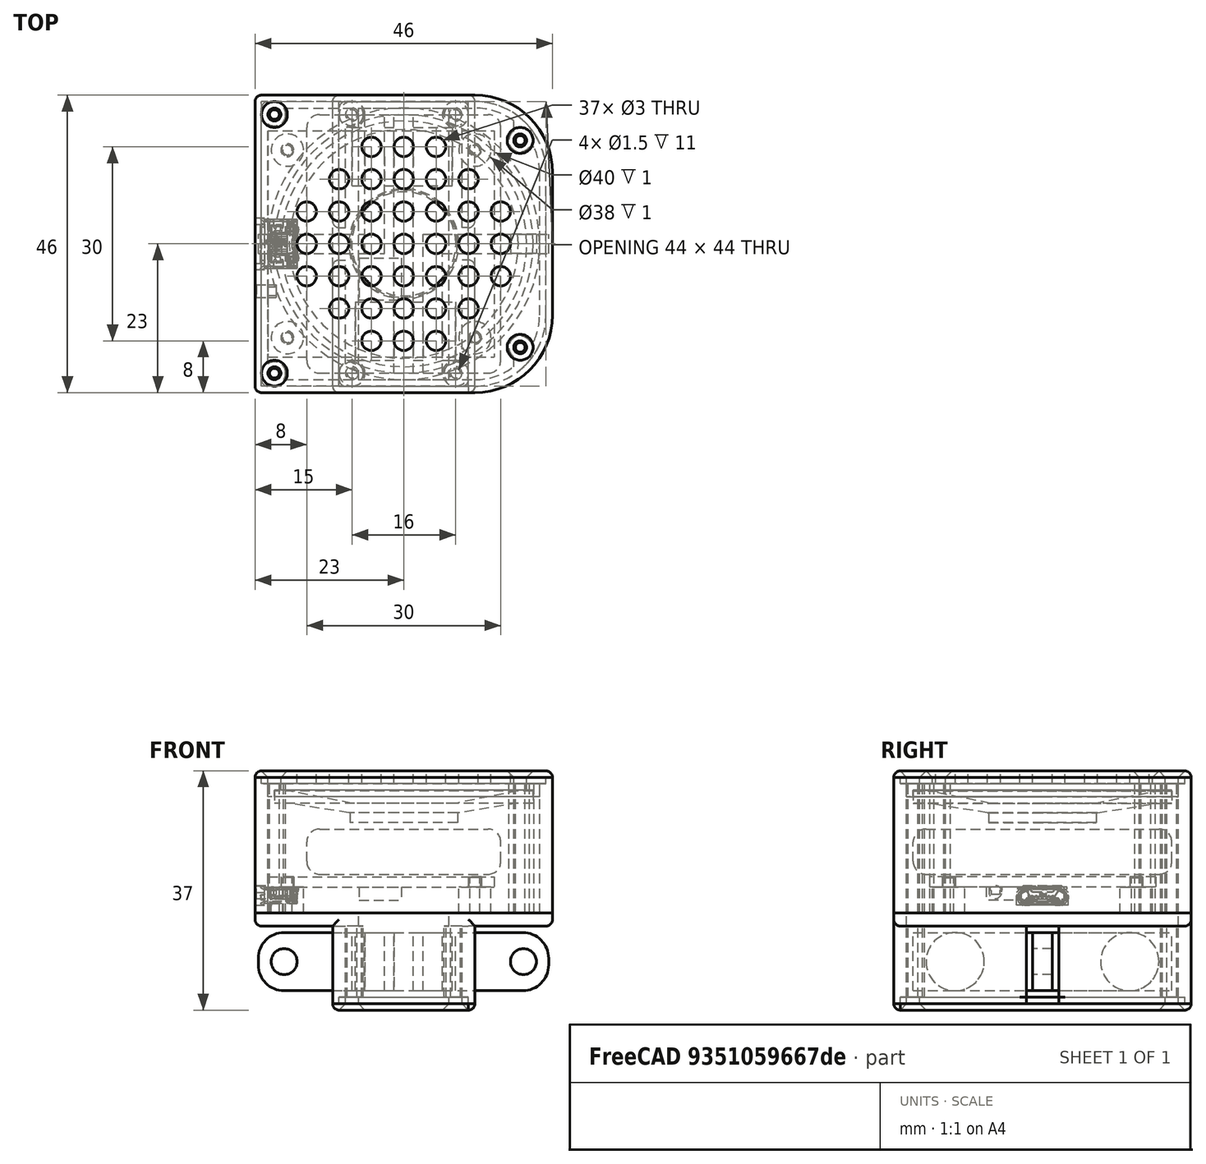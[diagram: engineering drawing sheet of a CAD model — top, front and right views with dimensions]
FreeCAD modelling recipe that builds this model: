
FCSTD DOCUMENT  (FreeCAD 0.19R)
Label: NoPullShit
License: All rights reserved
LicenseURL: http://en.wikipedia.org/wiki/All_rights_reserved
objects: Part::Cylinder×88, Part::Box×36, Part::Cut×32, Part::Fillet×21, Part::MultiFuse×20, Part::Chamfer×3, Part::Cone×2, Part::Feature×1
note: 203 computed .brp shape members not serialized (recipe doc carries the construction recipe); baked Part::Feature solids carry a one-line shape summary decoded from their .brp

FEATURE [Part::Box] Box  label="BatteryCube"
  AttacherType = Attacher::AttachEngine3D
  Height = 7
  Length = 30
  Placement = pos=(-15,-20,21) rot=(0,0,1;0rad)
  Width = 40
FEATURE [Part::Box] Box001  label="FR4"
  AttacherType = Attacher::AttachEngine3D
  Height = 1.6
  Length = 35
  Width = 35
FEATURE [Part::Feature] Solid  label="10103594_AFCI_SW0001"
  Placement = pos=(3,17.5,3.8) rot=(0.57735,0.57735,-0.57735;4.18879rad)
  shape: bbox 6.034 x 8.041 x 3.601 mm, 793 faces (baked)
FEATURE [Part::Box] Box002  label="LEDa"
  AttacherType = Attacher::AttachEngine3D
  Height = 0.5
  Length = 1.25
  Width = 2
FEATURE [Part::Box] Box003  label="LEDb"
  AttacherType = Attacher::AttachEngine3D
  Height = 0.6
  Length = 1.25
  Placement = pos=(0,0.35,0.5) rot=(0,0,1;0rad)
  Width = 1.3
FEATURE [Part::MultiFuse] Fusion001  label="LED"
  Placement = pos=(0,23.792,1.6) rot=(0,0,1;0rad)
  Shapes = -> [Box002,Box003]
FEATURE [Part::Cylinder] Cylinder002  label="MH1"
  Angle = 360
  AttacherType = Attacher::AttachEngine3D
  Height = 1.6
  Placement = pos=(3,3,0) rot=(0,0,1;0rad)
  Radius = 1
FEATURE [Part::Cylinder] Cylinder003  label="MH2"
  Angle = 360
  AttacherType = Attacher::AttachEngine3D
  Height = 1.6
  Placement = pos=(32,3,0) rot=(0,0,1;0rad)
  Radius = 1
FEATURE [Part::Cylinder] Cylinder004  label="MH3"
  Angle = 360
  AttacherType = Attacher::AttachEngine3D
  Height = 1.6
  Placement = pos=(3,32,0) rot=(0,0,1;0rad)
  Radius = 1
FEATURE [Part::Cylinder] Cylinder005  label="MH4"
  Angle = 360
  AttacherType = Attacher::AttachEngine3D
  Height = 1.6
  Placement = pos=(32,32,0) rot=(0,0,1;0rad)
  Radius = 1
FEATURE [Part::MultiFuse] Fusion002  label="Holes"
  Shapes = -> [Cylinder002,Cylinder003,Cylinder004,Cylinder005]
FEATURE [Part::Cut] Cut
  Base = -> Box001
  Tool = -> Fusion002
FEATURE [Part::Box] Box004  label="MCU"
  AttacherType = Attacher::AttachEngine3D
  Height = 2
  Length = 6.5
  Placement = pos=(14.1,19.7,1.6) rot=(0,0,1;0rad)
  Width = 6.5
FEATURE [Part::MultiFuse] Fusion003  label="Board"
  Placement = pos=(-21,17.5,20.6) rot=(1,0,0;3.14159rad)
  Shapes = -> [Box004,Solid,Fusion001,Cut]
FEATURE [Part::Box] Box005  label="Cube"
  AttacherType = Attacher::AttachEngine3D
  Height = 9
  Length = 3
  Width = 40
FEATURE [Part::Box] Box006  label="Cube001"
  AttacherType = Attacher::AttachEngine3D
  Height = 9
  Length = 3
  Placement = pos=(4.5,0,0) rot=(0,0,1;0rad)
  Width = 21.5
FEATURE [Part::Box] Box007  label="Cube002"
  AttacherType = Attacher::AttachEngine3D
  Height = 9
  Length = 3
  Placement = pos=(-4.5,18.5,0) rot=(0,0,1;0rad)
  Width = 21.5
FEATURE [Part::Cylinder] Cylinder006
  Angle = 360
  AttacherType = Attacher::AttachEngine3D
  Height = 15.5
  Placement = pos=(-6,6.5,4.5) rot=(0,1,0;1.5708rad)
  Radius = 4.5
FEATURE [Part::Cylinder] Cylinder007
  Angle = 360
  AttacherType = Attacher::AttachEngine3D
  Height = 15.5
  Placement = pos=(-6.5,33.5,4.5) rot=(0,1,0;1.5708rad)
  Radius = 4.5
FEATURE [Part::Box] Box008  label="Cube003"
  AttacherType = Attacher::AttachEngine3D
  Height = 9
  Length = 16.4
  Placement = pos=(-21,18.5,0) rot=(0,0,1;0rad)
  Width = 3
FEATURE [Part::Box] Box009  label="Cube004"
  AttacherType = Attacher::AttachEngine3D
  Height = 9
  Length = 16.4
  Placement = pos=(7.5,18.5,0) rot=(0,0,1;0rad)
  Width = 3
FEATURE [Part::MultiFuse] Fusion004  label="Solid"
  Placement = pos=(-1.5,0,0) rot=(0,0,1;0rad)
  Shapes = -> [Box005,Box006,Box007,Cylinder006,Cylinder007,Box008,Box009]
FEATURE [Part::Cylinder] Cylinder008
  Angle = 360
  AttacherType = Attacher::AttachEngine3D
  Height = 10
  Placement = pos=(-18.5,25,4.5) rot=(1,0,0;1.5708rad)
  Radius = 2
FEATURE [Part::Cylinder] Cylinder009
  Angle = 360
  AttacherType = Attacher::AttachEngine3D
  Height = 10
  Placement = pos=(18.5,25,4.5) rot=(1,0,0;1.5708rad)
  Radius = 2
FEATURE [Part::MultiFuse] Fusion005  label="Holes001"
  Shapes = -> [Cylinder009,Cylinder008]
FEATURE [Part::Cut] Cut001  label="Solid001"
  Base = -> Fusion004
  Placement = pos=(0,-20,3) rot=(0,0,1;0rad)
  Tool = -> Fusion005
FEATURE [Part::Cylinder] Cylinder029
  Angle = 360
  AttacherType = Attacher::AttachEngine3D
  Height = 4
  Placement = pos=(-18,-14.5,15) rot=(0,0,1;0rad)
  Radius = 2.5
FEATURE [Part::Cylinder] Cylinder030
  Angle = 360
  AttacherType = Attacher::AttachEngine3D
  Height = 1.5
  Placement = pos=(-18,-14.5,19) rot=(0,0,1;0rad)
  Radius = 0.9
FEATURE [Part::Cylinder] Cylinder031
  Angle = 360
  AttacherType = Attacher::AttachEngine3D
  Height = 5.5
  Placement = pos=(-18,-14.5,15) rot=(0,0,1;0rad)
  Radius = 0.75
FEATURE [Part::MultiFuse] Fusion006
  Shapes = -> [Cylinder029,Cylinder030]
FEATURE [Part::Cut] Cut006  label="Support1"
  Base = -> Fusion006
  Tool = -> Cylinder031
FEATURE [Part::Cylinder] Cylinder032
  Angle = 360
  AttacherType = Attacher::AttachEngine3D
  Height = 4
  Placement = pos=(-18,-14.5,15) rot=(0,0,1;0rad)
  Radius = 2.5
FEATURE [Part::Cylinder] Cylinder033
  Angle = 360
  AttacherType = Attacher::AttachEngine3D
  Height = 1.5
  Placement = pos=(-18,-14.5,19) rot=(0,0,1;0rad)
  Radius = 0.9
FEATURE [Part::MultiFuse] Fusion007
  Shapes = -> [Cylinder032,Cylinder033]
FEATURE [Part::Cylinder] Cylinder034
  Angle = 360
  AttacherType = Attacher::AttachEngine3D
  Height = 5.5
  Placement = pos=(-18,-14.5,15) rot=(0,0,1;0rad)
  Radius = 0.75
FEATURE [Part::Cut] Cut007  label="Support2"
  Base = -> Fusion007
  Placement = pos=(29,0,0) rot=(0,0,1;0rad)
  Tool = -> Cylinder034
FEATURE [Part::Cylinder] Cylinder035
  Angle = 360
  AttacherType = Attacher::AttachEngine3D
  Height = 4
  Placement = pos=(-18,-14.5,15) rot=(0,0,1;0rad)
  Radius = 2.5
FEATURE [Part::Cylinder] Cylinder036
  Angle = 360
  AttacherType = Attacher::AttachEngine3D
  Height = 1.5
  Placement = pos=(-18,-14.5,19) rot=(0,0,1;0rad)
  Radius = 0.9
FEATURE [Part::MultiFuse] Fusion008
  Shapes = -> [Cylinder035,Cylinder036]
FEATURE [Part::Cylinder] Cylinder037
  Angle = 360
  AttacherType = Attacher::AttachEngine3D
  Height = 5.5
  Placement = pos=(-18,-14.5,15) rot=(0,0,1;0rad)
  Radius = 0.75
FEATURE [Part::Cut] Cut008  label="Support3"
  Base = -> Fusion008
  Placement = pos=(29,29,0) rot=(0,0,1;0rad)
  Tool = -> Cylinder037
FEATURE [Part::Cylinder] Cylinder038
  Angle = 360
  AttacherType = Attacher::AttachEngine3D
  Height = 4
  Placement = pos=(-18,-14.5,15) rot=(0,0,1;0rad)
  Radius = 2.5
FEATURE [Part::Cylinder] Cylinder039
  Angle = 360
  AttacherType = Attacher::AttachEngine3D
  Height = 1.5
  Placement = pos=(-18,-14.5,19) rot=(0,0,1;0rad)
  Radius = 0.9
FEATURE [Part::MultiFuse] Fusion009
  Shapes = -> [Cylinder038,Cylinder039]
FEATURE [Part::Cylinder] Cylinder040
  Angle = 360
  AttacherType = Attacher::AttachEngine3D
  Height = 5.5
  Placement = pos=(-18,-14.5,15) rot=(0,0,1;0rad)
  Radius = 0.75
FEATURE [Part::Cut] Cut009  label="Support4"
  Base = -> Fusion009
  Placement = pos=(0,29,0) rot=(0,0,1;0rad)
  Tool = -> Cylinder040
FEATURE [Part::Fillet] Fillet  label="Battery"
  Base = -> Box
  Edges = 12 edges r=2: [Edge1,Edge2,Edge3,Edge4,Edge5,Edge6,Edge7,Edge8,Edge9,Edge10,Edge11,Edge12]
FEATURE [Part::MultiFuse] Fusion022  label="PcbSupport"
  Shapes = -> [Cut006,Cut007,Cut008,Cut009]
FEATURE [Part::Fillet] Fillet009  label="LoadCell"
  Base = -> Cut001
  Edges = 4 edges r=4: [Edge82,Edge89,Edge102,Edge104]
FEATURE [Part::Cylinder] Cylinder128
  Angle = 360
  AttacherType = Attacher::AttachEngine3D
  Height = 1.9
  Radius = 20
FEATURE [Part::Cone] Cone001
  Angle = 360
  AttacherType = Attacher::AttachEngine3D
  Height = 1.5
  Placement = pos=(0,0,1.9) rot=(0,0,1;0rad)
  Radius1 = 17.7
  Radius2 = 8.5
FEATURE [Part::Cylinder] Cylinder129
  Angle = 360
  AttacherType = Attacher::AttachEngine3D
  Height = 1.5
  Placement = pos=(0,0,3.4) rot=(0,0,1;0rad)
  Radius = 8.3
FEATURE [Part::Cone] Cone002
  Angle = 360
  AttacherType = Attacher::AttachEngine3D
  Height = 2.5
  Radius1 = 17.7
  Radius2 = 5
FEATURE [Part::Cut] Cut034
  Base = -> Cylinder128
  Tool = -> Cone002
FEATURE [Part::MultiFuse] Fusion025  label="Speaker"
  Placement = pos=(0,0,33.9) rot=(1,0,0;3.14159rad)
  Shapes = -> [Cone001,Cylinder129,Cut034]
FEATURE [Part::Box] Box078  label="Cube073"
  AttacherType = Attacher::AttachEngine3D
  Height = 2
  Length = 22
  Placement = pos=(-11,-23,0) rot=(0,0,1;0rad)
  Width = 46
FEATURE [Part::Cylinder] Cylinder209
  Angle = 360
  AttacherType = Attacher::AttachEngine3D
  Height = 11
  Placement = pos=(-8,-20,-3) rot=(0,0,1;0rad)
  Radius = 1
FEATURE [Part::Cylinder] Cylinder210
  Angle = 360
  AttacherType = Attacher::AttachEngine3D
  Height = 11
  Placement = pos=(8,-20,-3) rot=(0,0,1;0rad)
  Radius = 1
FEATURE [Part::Cylinder] Cylinder211
  Angle = 360
  AttacherType = Attacher::AttachEngine3D
  Height = 11
  Placement = pos=(-8,20,-3) rot=(0,0,1;0rad)
  Radius = 1
FEATURE [Part::Cylinder] Cylinder212
  Angle = 360
  AttacherType = Attacher::AttachEngine3D
  Height = 11
  Placement = pos=(8,20,-3) rot=(0,0,1;0rad)
  Radius = 1
FEATURE [Part::MultiFuse] Fusion039
  Shapes = -> [Cylinder209,Cylinder210,Cylinder211,Cylinder212]
FEATURE [Part::Cut] Cut063
  Base = -> Box078
  Tool = -> Fusion039
FEATURE [Part::Chamfer] Chamfer008
  Base = -> Cut063
  Edges = 4 edges r=1: [Edge17,Edge18,Edge19,Edge20]
FEATURE [Part::Fillet] Fillet028
  Base = -> Chamfer008
  Edges = 8 edges r=1: [Edge2,Edge3,Edge4,Edge5,Edge11,Edge13,Edge14,Edge16]
FEATURE [Part::Box] Box079  label="Cube074"
  AttacherType = Attacher::AttachEngine3D
  Height = 1
  Length = 20
  Placement = pos=(-10,-22,1) rot=(0,0,1;0rad)
  Width = 44
FEATURE [Part::Box] Box080  label="Cube075"
  AttacherType = Attacher::AttachEngine3D
  Height = 1
  Length = 22
  Placement = pos=(-11,-23,1) rot=(0,0,1;0rad)
  Width = 46
FEATURE [Part::Cut] Cut064
  Base = -> Box080
  Tool = -> Box079
FEATURE [Part::Box] Box085  label="Cube080"
  AttacherType = Attacher::AttachEngine3D
  Height = 2
  Length = 14
  Placement = pos=(-7,-21,13) rot=(0,0,1;0rad)
  Width = 42
FEATURE [Part::Box] Box086  label="Cube081"
  AttacherType = Attacher::AttachEngine3D
  Height = 2
  Length = 46
  Placement = pos=(-23,-23,13) rot=(0,0,1;0rad)
  Width = 46
FEATURE [Part::Fillet] Fillet030
  Base = -> Box086
  Edges = 2 edges r=1: [Edge1,Edge3]
FEATURE [Part::Fillet] Fillet029
  Base = -> Fillet030
  Edges = 2 edges r=12: [Edge17,Edge18]
FEATURE [Part::Cut] Cut066
  Base = -> Fillet029
  Tool = -> Box085
FEATURE [Part::Box] Box087  label="Cube082"
  AttacherType = Attacher::AttachEngine3D
  Height = 12
  Length = 22
  Placement = pos=(-11,-23,1) rot=(0,0,1;0rad)
  Width = 2
FEATURE [Part::Box] Box088  label="Cube083"
  AttacherType = Attacher::AttachEngine3D
  Height = 12
  Length = 22
  Placement = pos=(-11,21,1) rot=(0,0,1;0rad)
  Width = 2
FEATURE [Part::Box] Box089  label="Cube084"
  AttacherType = Attacher::AttachEngine3D
  Height = 12
  Length = 2
  Placement = pos=(-11,-23,1) rot=(0,0,1;0rad)
  Width = 20.5
FEATURE [Part::Box] Box090  label="Cube085"
  AttacherType = Attacher::AttachEngine3D
  Height = 12
  Length = 2
  Placement = pos=(9,-23,1) rot=(0,0,1;0rad)
  Width = 20.5
FEATURE [Part::Box] Box091  label="Cube086"
  AttacherType = Attacher::AttachEngine3D
  Height = 12
  Length = 2
  Placement = pos=(-11,2.5,1) rot=(0,0,1;0rad)
  Width = 20.5
FEATURE [Part::Box] Box092  label="Cube087"
  AttacherType = Attacher::AttachEngine3D
  Height = 12
  Length = 2
  Placement = pos=(9,2.5,1) rot=(0,0,1;0rad)
  Width = 20.5
FEATURE [Part::Cylinder] Cylinder213
  Angle = 360
  AttacherType = Attacher::AttachEngine3D
  Height = 11
  Placement = pos=(-8,-20,2) rot=(0,0,1;0rad)
  Radius = 1.75
FEATURE [Part::Cylinder] Cylinder214
  Angle = 360
  AttacherType = Attacher::AttachEngine3D
  Height = 11
  Placement = pos=(8,-20,2) rot=(0,0,1;0rad)
  Radius = 1.75
FEATURE [Part::Cylinder] Cylinder215
  Angle = 360
  AttacherType = Attacher::AttachEngine3D
  Height = 11
  Placement = pos=(-8,20,2) rot=(0,0,1;0rad)
  Radius = 1.75
FEATURE [Part::Cylinder] Cylinder216
  Angle = 360
  AttacherType = Attacher::AttachEngine3D
  Height = 11
  Placement = pos=(8,20,2) rot=(0,0,1;0rad)
  Radius = 1.75
FEATURE [Part::Cylinder] Cylinder217
  Angle = 360
  AttacherType = Attacher::AttachEngine3D
  Height = 11
  Placement = pos=(-8,-20,2) rot=(0,0,1;0rad)
  Radius = 0.75
FEATURE [Part::Cylinder] Cylinder218
  Angle = 360
  AttacherType = Attacher::AttachEngine3D
  Height = 11
  Placement = pos=(8,-20,2) rot=(0,0,1;0rad)
  Radius = 0.75
FEATURE [Part::Cylinder] Cylinder219
  Angle = 360
  AttacherType = Attacher::AttachEngine3D
  Height = 11
  Placement = pos=(-8,20,2) rot=(0,0,1;0rad)
  Radius = 0.75
FEATURE [Part::Cylinder] Cylinder220
  Angle = 360
  AttacherType = Attacher::AttachEngine3D
  Height = 11
  Placement = pos=(8,20,2) rot=(0,0,1;0rad)
  Radius = 0.75
FEATURE [Part::Cut] Cut067
  Base = -> Cylinder213
  Tool = -> Cylinder217
FEATURE [Part::Cut] Cut068
  Base = -> Cylinder214
  Tool = -> Cylinder218
FEATURE [Part::Cut] Cut069
  Base = -> Cylinder215
  Tool = -> Cylinder219
FEATURE [Part::Cut] Cut070
  Base = -> Cylinder216
  Tool = -> Cylinder220
FEATURE [Part::Box] Box093  label="Cube088"
  AttacherType = Attacher::AttachEngine3D
  Height = 1
  Length = 20
  Placement = pos=(-10,-22,1) rot=(0,0,1;0rad)
  Width = 44
FEATURE [Part::Box] Box094  label="Cube089"
  AttacherType = Attacher::AttachEngine3D
  Height = 10
  Length = 29
  Placement = pos=(-13,-2.5,0) rot=(0,0,1;0rad)
  Width = 5
FEATURE [Part::Box] Box095  label="Cube090"
  AttacherType = Attacher::AttachEngine3D
  Height = 1
  Length = 18
  Placement = pos=(-9,-21,1) rot=(0,0,1;0rad)
  Width = 42
FEATURE [Part::Cut] Cut072
  Base = -> Box093
  Tool = -> Box095
FEATURE [Part::Cut] Cut071
  Base = -> Cut072
  Tool = -> Box094
FEATURE [Part::Box] Box103  label="Cube098"
  AttacherType = Attacher::AttachEngine3D
  Height = 2
  Length = 46
  Placement = pos=(-23,-23,35) rot=(0,0,1;0rad)
  Width = 46
FEATURE [Part::Cylinder] Cylinder266
  Angle = 360
  AttacherType = Attacher::AttachEngine3D
  Height = 10
  Placement = pos=(0,0,31) rot=(0,0,1;0rad)
  Radius = 1.5
FEATURE [Part::Cylinder] Cylinder267
  Angle = 360
  AttacherType = Attacher::AttachEngine3D
  Height = 10
  Placement = pos=(5,0,31) rot=(0,0,1;0rad)
  Radius = 1.5
FEATURE [Part::Cylinder] Cylinder268
  Angle = 360
  AttacherType = Attacher::AttachEngine3D
  Height = 10
  Placement = pos=(10,0,31) rot=(0,0,1;0rad)
  Radius = 1.5
FEATURE [Part::Cylinder] Cylinder269
  Angle = 360
  AttacherType = Attacher::AttachEngine3D
  Height = 10
  Placement = pos=(15,0,31) rot=(0,0,1;0rad)
  Radius = 1.5
FEATURE [Part::Cylinder] Cylinder270
  Angle = 360
  AttacherType = Attacher::AttachEngine3D
  Height = 10
  Placement = pos=(-5,0,31) rot=(0,0,1;0rad)
  Radius = 1.5
FEATURE [Part::Cylinder] Cylinder271
  Angle = 360
  AttacherType = Attacher::AttachEngine3D
  Height = 10
  Placement = pos=(-10,0,31) rot=(0,0,1;0rad)
  Radius = 1.5
FEATURE [Part::Cylinder] Cylinder272
  Angle = 360
  AttacherType = Attacher::AttachEngine3D
  Height = 10
  Placement = pos=(-15,0,31) rot=(0,0,1;0rad)
  Radius = 1.5
FEATURE [Part::Cylinder] Cylinder273
  Angle = 360
  AttacherType = Attacher::AttachEngine3D
  Height = 10
  Placement = pos=(0,5,31) rot=(0,0,1;0rad)
  Radius = 1.5
FEATURE [Part::Cylinder] Cylinder274
  Angle = 360
  AttacherType = Attacher::AttachEngine3D
  Height = 10
  Placement = pos=(0,10,31) rot=(0,0,1;0rad)
  Radius = 1.5
FEATURE [Part::Cylinder] Cylinder275
  Angle = 360
  AttacherType = Attacher::AttachEngine3D
  Height = 10
  Placement = pos=(0,15,31) rot=(0,0,1;0rad)
  Radius = 1.5
FEATURE [Part::Cylinder] Cylinder276
  Angle = 360
  AttacherType = Attacher::AttachEngine3D
  Height = 10
  Placement = pos=(0,-5,31) rot=(0,0,1;0rad)
  Radius = 1.5
FEATURE [Part::Cylinder] Cylinder277
  Angle = 360
  AttacherType = Attacher::AttachEngine3D
  Height = 10
  Placement = pos=(0,-10,31) rot=(0,0,1;0rad)
  Radius = 1.5
FEATURE [Part::Cylinder] Cylinder278
  Angle = 360
  AttacherType = Attacher::AttachEngine3D
  Height = 10
  Placement = pos=(0,-15,31) rot=(0,0,1;0rad)
  Radius = 1.5
FEATURE [Part::Cylinder] Cylinder279
  Angle = 360
  AttacherType = Attacher::AttachEngine3D
  Height = 10
  Placement = pos=(5,5,31) rot=(0,0,1;0rad)
  Radius = 1.5
FEATURE [Part::Cylinder] Cylinder280
  Angle = 360
  AttacherType = Attacher::AttachEngine3D
  Height = 10
  Placement = pos=(10,5,31) rot=(0,0,1;0rad)
  Radius = 1.5
FEATURE [Part::Cylinder] Cylinder281
  Angle = 360
  AttacherType = Attacher::AttachEngine3D
  Height = 10
  Placement = pos=(15,5,31) rot=(0,0,1;0rad)
  Radius = 1.5
FEATURE [Part::Cylinder] Cylinder282
  Angle = 360
  AttacherType = Attacher::AttachEngine3D
  Height = 10
  Placement = pos=(10,10,31) rot=(0,0,1;0rad)
  Radius = 1.5
FEATURE [Part::Cylinder] Cylinder283
  Angle = 360
  AttacherType = Attacher::AttachEngine3D
  Height = 10
  Placement = pos=(5,10,31) rot=(0,0,1;0rad)
  Radius = 1.5
FEATURE [Part::Cylinder] Cylinder284
  Angle = 360
  AttacherType = Attacher::AttachEngine3D
  Height = 10
  Placement = pos=(-5,10,31) rot=(0,0,1;0rad)
  Radius = 1.5
FEATURE [Part::Cylinder] Cylinder285
  Angle = 360
  AttacherType = Attacher::AttachEngine3D
  Height = 10
  Placement = pos=(-10,10,31) rot=(0,0,1;0rad)
  Radius = 1.5
FEATURE [Part::Cylinder] Cylinder286
  Angle = 360
  AttacherType = Attacher::AttachEngine3D
  Height = 10
  Placement = pos=(-15,5,31) rot=(0,0,1;0rad)
  Radius = 1.5
FEATURE [Part::Cylinder] Cylinder287
  Angle = 360
  AttacherType = Attacher::AttachEngine3D
  Height = 10
  Placement = pos=(-10,5,31) rot=(0,0,1;0rad)
  Radius = 1.5
FEATURE [Part::Cylinder] Cylinder288
  Angle = 360
  AttacherType = Attacher::AttachEngine3D
  Height = 10
  Placement = pos=(-5,5,31) rot=(0,0,1;0rad)
  Radius = 1.5
FEATURE [Part::Cylinder] Cylinder289
  Angle = 360
  AttacherType = Attacher::AttachEngine3D
  Height = 10
  Placement = pos=(-5,15,31) rot=(0,0,1;0rad)
  Radius = 1.5
FEATURE [Part::Cylinder] Cylinder290
  Angle = 360
  AttacherType = Attacher::AttachEngine3D
  Height = 10
  Placement = pos=(5,15,31) rot=(0,0,1;0rad)
  Radius = 1.5
FEATURE [Part::Cylinder] Cylinder291
  Angle = 360
  AttacherType = Attacher::AttachEngine3D
  Height = 10
  Placement = pos=(5,-15,31) rot=(0,0,1;0rad)
  Radius = 1.5
FEATURE [Part::Cylinder] Cylinder292
  Angle = 360
  AttacherType = Attacher::AttachEngine3D
  Height = 10
  Placement = pos=(-5,-15,31) rot=(0,0,1;0rad)
  Radius = 1.5
FEATURE [Part::Cylinder] Cylinder293
  Angle = 360
  AttacherType = Attacher::AttachEngine3D
  Height = 10
  Placement = pos=(-5,-5,31) rot=(0,0,1;0rad)
  Radius = 1.5
FEATURE [Part::Cylinder] Cylinder294
  Angle = 360
  AttacherType = Attacher::AttachEngine3D
  Height = 10
  Placement = pos=(-10,-5,31) rot=(0,0,1;0rad)
  Radius = 1.5
FEATURE [Part::Cylinder] Cylinder295
  Angle = 360
  AttacherType = Attacher::AttachEngine3D
  Height = 10
  Placement = pos=(-15,-5,31) rot=(0,0,1;0rad)
  Radius = 1.5
FEATURE [Part::Cylinder] Cylinder296
  Angle = 360
  AttacherType = Attacher::AttachEngine3D
  Height = 10
  Placement = pos=(-10,-10,31) rot=(0,0,1;0rad)
  Radius = 1.5
FEATURE [Part::Cylinder] Cylinder297
  Angle = 360
  AttacherType = Attacher::AttachEngine3D
  Height = 10
  Placement = pos=(-5,-10,31) rot=(0,0,1;0rad)
  Radius = 1.5
FEATURE [Part::Cylinder] Cylinder298
  Angle = 360
  AttacherType = Attacher::AttachEngine3D
  Height = 10
  Placement = pos=(5,-10,31) rot=(0,0,1;0rad)
  Radius = 1.5
FEATURE [Part::Cylinder] Cylinder299
  Angle = 360
  AttacherType = Attacher::AttachEngine3D
  Height = 10
  Placement = pos=(10,-10,31) rot=(0,0,1;0rad)
  Radius = 1.5
FEATURE [Part::Cylinder] Cylinder300
  Angle = 360
  AttacherType = Attacher::AttachEngine3D
  Height = 10
  Placement = pos=(15,-5,31) rot=(0,0,1;0rad)
  Radius = 1.5
FEATURE [Part::Cylinder] Cylinder301
  Angle = 360
  AttacherType = Attacher::AttachEngine3D
  Height = 10
  Placement = pos=(10,-5,31) rot=(0,0,1;0rad)
  Radius = 1.5
FEATURE [Part::Cylinder] Cylinder302
  Angle = 360
  AttacherType = Attacher::AttachEngine3D
  Height = 10
  Placement = pos=(5,-5,31) rot=(0,0,1;0rad)
  Radius = 1.5
FEATURE [Part::MultiFuse] Fusion050  label="SpeakerHoles003"
  Shapes = -> [Cylinder302,Cylinder266,Cylinder267,Cylinder268,Cylinder269,Cylinder270,Cylinder271,Cylinder272,Cylinder273,Cylinder274,Cylinder275,Cylinder276,Cylinder277,Cylinder278,Cylinder279,Cylinder280,Cylinder281,Cylinder282,Cylinder283,Cylinder284,Cylinder285,Cylinder286,Cylinder287,Cylinder288,Cylinder289,Cylinder290,Cylinder291,Cylinder292,Cylinder293,Cylinder294,Cylinder295,Cylinder296,Cylinder297,+4 more]
FEATURE [Part::Cut] Cut080  label="Perf003"
  Base = -> Box103
  Tool = -> Fusion050
FEATURE [Part::Fillet] Fillet043
  Base = -> Cut080
  Edges = 2 edges r=1: [Edge1,Edge3]
FEATURE [Part::Fillet] Fillet044
  Base = -> Fillet043
  Edges = 2 edges r=12: [Edge91,Edge92]
FEATURE [Part::Fillet] Fillet045
  Base = -> Fillet044
  Edges = 8 edges r=1: [Edge1,Edge2,Edge3,Edge4,Edge5,Edge6,Edge7,Edge8]
FEATURE [Part::Cylinder] Cylinder303
  Angle = 360
  AttacherType = Attacher::AttachEngine3D
  Height = 2
  Placement = pos=(0,0,35) rot=(0,0,1;0rad)
  Radius = 21
FEATURE [Part::Cylinder] Cylinder304
  Angle = 360
  AttacherType = Attacher::AttachEngine3D
  Height = 2
  Placement = pos=(0,0,35) rot=(0,0,1;0rad)
  Radius = 20
FEATURE [Part::Cut] Cut081  label="SpeakerRing004"
  Base = -> Cylinder303
  Placement = pos=(0,0,-2) rot=(0,0,1;0rad)
  Tool = -> Cylinder304
FEATURE [Part::Cylinder] Cylinder305
  Angle = 360
  AttacherType = Attacher::AttachEngine3D
  Height = 1
  Radius = 20
FEATURE [Part::Cylinder] Cylinder306
  Angle = 360
  AttacherType = Attacher::AttachEngine3D
  Height = 1
  Radius = 19
FEATURE [Part::Cut] Cut082
  Base = -> Cylinder305
  Placement = pos=(0,0,34) rot=(0,0,1;0rad)
  Tool = -> Cylinder306
FEATURE [Part::MultiFuse] Fusion051  label="SpeakerHolder004"
  Shapes = -> [Cut082,Cut081]
FEATURE [Part::Cylinder] Cylinder307
  Angle = 360
  AttacherType = Attacher::AttachEngine3D
  Height = 20
  Placement = pos=(18,16,19) rot=(0,0,1;0rad)
  Radius = 1
FEATURE [Part::Cylinder] Cylinder308
  Angle = 360
  AttacherType = Attacher::AttachEngine3D
  Height = 20
  Placement = pos=(-20,-20,19) rot=(0,0,1;0rad)
  Radius = 1
FEATURE [Part::Cylinder] Cylinder309
  Angle = 360
  AttacherType = Attacher::AttachEngine3D
  Height = 20
  Placement = pos=(18,-16,19) rot=(0,0,1;0rad)
  Radius = 1
FEATURE [Part::Cylinder] Cylinder310
  Angle = 360
  AttacherType = Attacher::AttachEngine3D
  Height = 20
  Placement = pos=(-20,20,19) rot=(0,0,1;0rad)
  Radius = 1
FEATURE [Part::MultiFuse] Fusion052
  Shapes = -> [Cylinder307,Cylinder308,Cylinder309,Cylinder310]
FEATURE [Part::Cut] Cut083
  Base = -> Fillet045
  Tool = -> Fusion052
FEATURE [Part::Chamfer] Chamfer010
  Base = -> Cut083
  Edges = 4 edges r=1: [Edge7,Edge16,Edge32,Edge47]
FEATURE [Part::MultiFuse] Fusion053
  Shapes = -> [Fusion051,Chamfer010]
FEATURE [Part::Box] Box106  label="Cube101"
  AttacherType = Attacher::AttachEngine3D
  Height = 20
  Length = 1.5
  Placement = pos=(19,-17,15) rot=(0,0,1;0rad)
  Width = 2
FEATURE [Part::Cylinder] Cylinder311
  Angle = 360
  AttacherType = Attacher::AttachEngine3D
  Height = 20
  Placement = pos=(-20,-20,15) rot=(0,0,1;0rad)
  Radius = 0.75
FEATURE [Part::Box] Box107  label="Cube102"
  AttacherType = Attacher::AttachEngine3D
  Height = 20
  Length = 2
  Placement = pos=(17,-19.5,15) rot=(0,0,1;0rad)
  Width = 2.5
FEATURE [Part::Box] Box108  label="Cube103"
  AttacherType = Attacher::AttachEngine3D
  Height = 20
  Length = 1.5
  Placement = pos=(19,15,15) rot=(0,0,1;0rad)
  Width = 2
FEATURE [Part::Box] Box109  label="Cube104"
  AttacherType = Attacher::AttachEngine3D
  Height = 3
  Length = 10
  Placement = pos=(-23,-4,16.2) rot=(0,0,1;0rad)
  Width = 8
FEATURE [Part::Chamfer] Chamfer011
  Base = -> Box109
  Edges = 2 edges r=1: [Edge10,Edge12]
FEATURE [Part::Cylinder] Cylinder312
  Angle = 360
  AttacherType = Attacher::AttachEngine3D
  Height = 10
  Placement = pos=(-22.8,-7.29,18.25) rot=(0,1,0;1.5708rad)
  Radius = 1
FEATURE [Part::Cylinder] Cylinder313
  Angle = 360
  AttacherType = Attacher::AttachEngine3D
  Height = 20
  Placement = pos=(-20,-20,15) rot=(0,0,1;0rad)
  Radius = 0.75
FEATURE [Part::Box] Box110  label="Cube105"
  AttacherType = Attacher::AttachEngine3D
  Height = 20
  Length = 2
  Placement = pos=(17,17,15) rot=(0,0,1;0rad)
  Width = 2.5
FEATURE [Part::Cylinder] Cylinder314
  Angle = 360
  AttacherType = Attacher::AttachEngine3D
  Height = 20
  Placement = pos=(-20,-20,15) rot=(0,0,1;0rad)
  Radius = 1.75
FEATURE [Part::Cut] Cut087
  Base = -> Cylinder314
  Tool = -> Cylinder311
FEATURE [Part::Box] Box111  label="Cube106"
  AttacherType = Attacher::AttachEngine3D
  Height = 20
  Length = 42
  Placement = pos=(-21,-21,15) rot=(0,0,1;0rad)
  Width = 42
FEATURE [Part::Fillet] Fillet048
  Base = -> Box111
  Edges = 2 edges r=10: [Edge5,Edge7]
FEATURE [Part::Cylinder] Cylinder315
  Angle = 360
  AttacherType = Attacher::AttachEngine3D
  Height = 20
  Placement = pos=(-20,-20,15) rot=(0,0,1;0rad)
  Radius = 1.75
FEATURE [Part::Cylinder] Cylinder316
  Angle = 360
  AttacherType = Attacher::AttachEngine3D
  Height = 20
  Placement = pos=(-20,-20,15) rot=(0,0,1;0rad)
  Radius = 0.75
FEATURE [Part::Box] Box112  label="Cube107"
  AttacherType = Attacher::AttachEngine3D
  Height = 20
  Length = 46
  Placement = pos=(-23,-23,15) rot=(0,0,1;0rad)
  Width = 46
FEATURE [Part::Cylinder] Cylinder317
  Angle = 360
  AttacherType = Attacher::AttachEngine3D
  Height = 20
  Placement = pos=(-20,-20,15) rot=(0,0,1;0rad)
  Radius = 0.75
FEATURE [Part::Fillet] Fillet049
  Base = -> Box112
  Edges = 2 edges r=12: [Edge5,Edge7]
FEATURE [Part::Cut] Cut086
  Base = -> Fillet049
  Tool = -> Fillet048
FEATURE [Part::Fillet] Fillet047
  Base = -> Cut086
  Edges = 2 edges r=1: [Edge29,Edge30]
FEATURE [Part::Cut] Cut085
  Base = -> Fillet047
  Tool = -> Chamfer011
FEATURE [Part::Cut] Cut088
  Base = -> Cut085
  Tool = -> Cylinder312
FEATURE [Part::Cylinder] Cylinder318
  Angle = 360
  AttacherType = Attacher::AttachEngine3D
  Height = 20
  Placement = pos=(-20,-20,15) rot=(0,0,1;0rad)
  Radius = 1.75
FEATURE [Part::Cut] Cut090
  Base = -> Cylinder318
  Placement = pos=(0,40,0) rot=(0,0,1;0rad)
  Tool = -> Cylinder317
FEATURE [Part::Cylinder] Cylinder319
  Angle = 360
  AttacherType = Attacher::AttachEngine3D
  Height = 20
  Placement = pos=(-20,-20,15) rot=(0,0,1;0rad)
  Radius = 1.75
FEATURE [Part::Cut] Cut089
  Base = -> Cylinder319
  Placement = pos=(38,4,0) rot=(0,0,1;0rad)
  Tool = -> Cylinder316
FEATURE [Part::Cut] Cut091
  Base = -> Cylinder315
  Placement = pos=(38,36,0) rot=(0,0,1;0rad)
  Tool = -> Cylinder313
FEATURE [Part::MultiFuse] Fusion056  label="RoundTopSection001"
  Shapes = -> [Cut091,Cut088,Cut087,Cut089,Cut090,Box107,Box108,Box106,Box110]
FEATURE [Part::Box] Box113  label="Cube108"
  AttacherType = Attacher::AttachEngine3D
  Height = 1
  Length = 46
  Placement = pos=(-23,-23,35) rot=(0,0,1;0rad)
  Width = 46
FEATURE [Part::Fillet] Fillet051
  Base = -> Box113
  Edges = 2 edges r=12: [Edge5,Edge7]
FEATURE [Part::Box] Box114  label="Cube109"
  AttacherType = Attacher::AttachEngine3D
  Height = 20
  Length = 44
  Placement = pos=(-22,-22,15) rot=(0,0,1;0rad)
  Width = 44
FEATURE [Part::Fillet] Fillet052
  Base = -> Box114
  Edges = 2 edges r=11: [Edge5,Edge7]
  Placement = pos=(0,0,2) rot=(0,0,1;0rad)
FEATURE [Part::Fillet] Fillet053
  Base = -> Fillet051
  Edges = 2 edges r=1: [Edge17,Edge18]
FEATURE [Part::Cut] Cut092
  Base = -> Fillet053
  Tool = -> Fillet052
FEATURE [Part::MultiFuse] Fusion  label="TopSection"
  Shapes = -> [Fusion056,Cut092]
FEATURE [Part::Box] Box117  label="Cube112"
  AttacherType = Attacher::AttachEngine3D
  Height = 20
  Length = 44
  Placement = pos=(-22,-22,15) rot=(0,0,1;0rad)
  Width = 44
FEATURE [Part::Fillet] Fillet058
  Base = -> Box117
  Edges = 2 edges r=11: [Edge5,Edge7]
  Placement = pos=(0,0,2) rot=(0,0,1;0rad)
FEATURE [Part::Box] Box118  label="Cube113"
  AttacherType = Attacher::AttachEngine3D
  Height = 1
  Length = 46
  Placement = pos=(-23,-23,35) rot=(0,0,1;0rad)
  Width = 46
FEATURE [Part::Fillet] Fillet059
  Base = -> Box118
  Edges = 2 edges r=12: [Edge5,Edge7]
FEATURE [Part::Fillet] Fillet057
  Base = -> Fillet059
  Edges = 2 edges r=1: [Edge17,Edge18]
FEATURE [Part::Cut] Cut094
  Base = -> Fillet057
  Tool = -> Fillet058
FEATURE [Part::Cut] Cut095
  Base = -> Fusion053
  Tool = -> Cut094
FEATURE [Part::MultiFuse] Fusion057
  Shapes = -> [Box087,Box088,Box089,Box090,Box091,Box092,Cut067,Cut068,Cut069,Cut070]
FEATURE [Part::Fillet] Fillet060
  Base = -> Fusion057
  Edges = 8 edges r=1: [Edge1,Edge12,Edge34,Edge78,Edge83,Edge87,Edge130,Edge159]
FEATURE [Part::MultiFuse] Fusion058
  Shapes = -> [Fillet060,Cut066]
FEATURE [Part::Fillet] Fillet061
  Base = -> Fusion058
  Edges = 4 edges r=1: [Edge6,Edge8,Edge23,Edge116]
FEATURE [Part::Cut] Cut096  label="BottomSection"
  Base = -> Fillet061
  Tool = -> Cut071
FEATURE [Part::Cut] Cut097
  Base = -> Fillet028
  Tool = -> Cut064
FEATURE [Part::Fillet] Fillet062  label="TopCover"
  Base = -> Cut095
  Edges = 2 edges r=1: [Edge181,Edge182]
FEATURE [Part::Fillet] Fillet063  label="BottomCover"
  Base = -> Cut097
  Edges = 4 edges r=1: [Edge62,Edge64,Edge65,Edge67]
